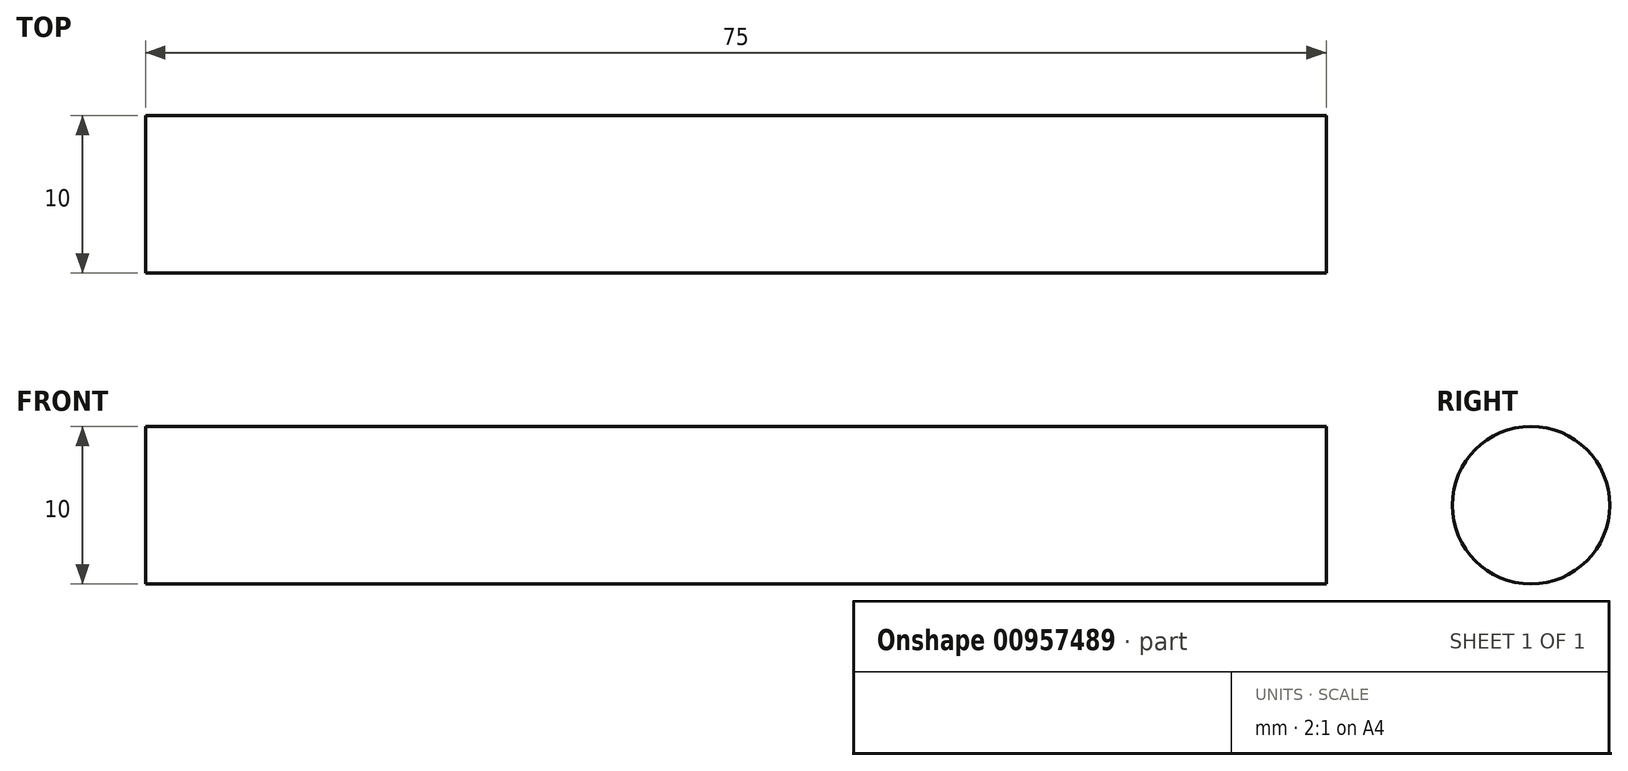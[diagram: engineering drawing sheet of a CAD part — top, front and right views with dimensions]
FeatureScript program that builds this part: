
annotation { "Feature Type Name" : "Feature", "Feature Type Description" : "" }
export const myFeature = defineFeature(function(context is Context, id is Id, definition is map)
    precondition{}
    {
        {
            var Q0;
            Q0=qCreatedBy(makeId("Front.planeOp"),FACE);
            var sketch = newSketch(context, id + "F0", { "sketchPlane" : qUnion([Q0])});
            skLineSegment(sketch, "E0", {"start": v(0, 0) * mm, "end": v(0, 5) * mm});
            skLineSegment(sketch, "E1", {"start": v(0, 5) * mm, "end": v(-75, 5) * mm});
            skLineSegment(sketch, "E2", {"start": v(-75, 5) * mm, "end": v(-75, 0) * mm});
            skLineSegment(sketch, "E3", {"start": v(-75, 0) * mm, "end": v(0, 0) * mm});
            skSolve(sketch);
        }
        {
            var Q0;
            Q0=makeQuery(id+"F0.imprint","IMPRINT",FACE,{"disambiguationData":[TD([[makeQuery(id+"F0.imprint","IMPRINT",EDGE,{"derivedFrom":sQuery(id+"F0.wireOp",EDGE,"E0")}),1.0]])]});
            var Q1;
            Q1=sQuery(id+"F0.wireOp",EDGE,"E3");
            revolve(context, id + "F1", {"surfaceOperationType" : NewSurfaceOperationType.NEW, "entities" : qUnion([Q0]), "axis" : qUnion([Q1]), "revolveType" : RevolveType.FULL});
        }
    });
